# Revit family: GFW No Sill L
name_source: partatom
category: Windows
revit_build: Autodesk Revit 2016 (Build: 20150714_1515(x64)
units: mm (PartAtom-declared; Revit-internal decimal feet)

## family parameters
Always vertical = Yes
Cut with Voids When Loaded = No
Host = Wall
Room Calculation Point = No
Shared = No

## types (1)
- GFW No Sill L
    Default Head Height = 2100 mm
    Description = Aluminum Fixed Window
    Frame Material = Aluminium
    Free Air = -2 mm  [stored -0.00656168 ft]
    Glass = Glass
    Height = 1200 mm
    Louvre Angle = 85.00°
    Louvre Depth = 150 mm
    Louvre Height = 150.3 mm
    Louvre Thickness = 10 mm  [stored 0.0328084 ft]
    Louvre Width = 828 mm  [stored 2.71654 ft]
    Manufacturer = Stegbar
    Material = Glass
    No of Louvres = 8
    Offset Exterior = 100 mm  [stored 0.328084 ft]
    Rough Height = 1220 mm  [stored 4.00262 ft]
    Rough Width = 910 mm
    Sash = Default
    Sill = Default
    Wall Closure = By host
    Width = 900 mm  [stored 2.95276 ft]

note: [stored X ft] marks values corroborated as IEEE doubles in the binary element streams (Revit-internal decimal feet)

## geometry (parser evidence)
native form markers: Extrusion x1, Sweep x25
no freeform markers — native parametric forms only
